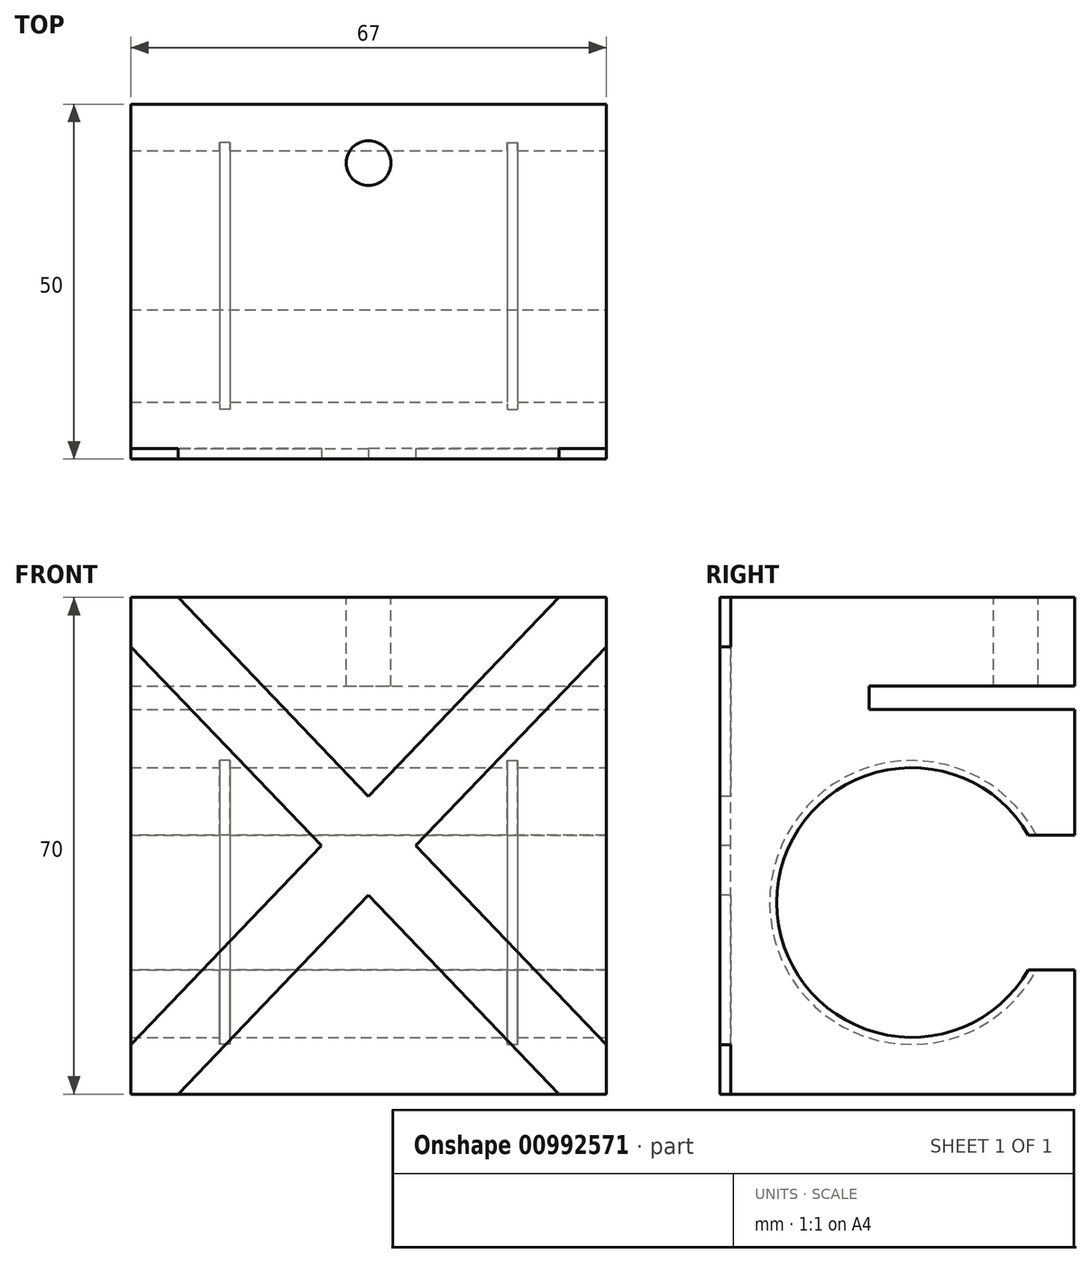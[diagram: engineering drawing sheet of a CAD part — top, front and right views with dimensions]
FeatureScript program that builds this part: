
annotation { "Feature Type Name" : "Feature", "Feature Type Description" : "" }
export const myFeature = defineFeature(function(context is Context, id is Id, definition is map)
    precondition{}
    {
        {
            var Q0;
            Q0=qCreatedBy(makeId("Top.planeOp"),FACE);
            var sketch = newSketch(context, id + "F0", { "sketchPlane" : qUnion([Q0])});
            skLineSegment(sketch, "E0.bottom", {"start": v(33.5, 25) * mm, "end": v(-33.5, 25) * mm});
            skLineSegment(sketch, "E0.top", {"start": v(33.5, -25) * mm, "end": v(-33.5, -25) * mm});
            skLineSegment(sketch, "E0.left", {"start": v(33.5, 25) * mm, "end": v(33.5, -25) * mm});
            skLineSegment(sketch, "E0.right", {"start": v(-33.5, 25) * mm, "end": v(-33.5, -25) * mm});
            skPoint(sketch, "E0.middle", {"position": v(0, 0) * mm});
            skSolve(sketch);
        }
        {
            var Q0;
            Q0 = qSketchRegion(id + "F0", true);
            extrude(context, id + "F1", {"entities" : qUnion([Q0]), "depth" : 70 * mm, "offsetDistance" : 25 * mm});
        }
        {
            var Q0;
            Q0=makeQuery(id+"F1.opExtrude","SWEPT_FACE",FACE,{"disambiguationData":[OSD([sQuery(id+"F0.wireOp",EDGE,"E0.top")])]});
            var sketch = newSketch(context, id + "F2", { "sketchPlane" : qUnion([Q0])});
            skLineSegment(sketch, "E1", {"start": v(-26.86, 70) * mm, "end": v(0, 41.94) * mm});
            skLineSegment(sketch, "E2", {"start": v(33.5, 6.94) * mm, "end": v(33.5, 0) * mm});
            skLineSegment(sketch, "E3", {"start": v(26.86, 0) * mm, "end": v(0, 28.06) * mm});
            skLineSegment(sketch, "E4", {"start": v(-33.5, 63.06) * mm, "end": v(-33.5, 70) * mm});
            skLineSegment(sketch, "E5", {"start": v(-33.5, 0) * mm, "end": v(-33.5, 6.94) * mm});
            skLineSegment(sketch, "E6", {"start": v(-33.5, 6.94) * mm, "end": v(-6.64, 35) * mm});
            skLineSegment(sketch, "E7", {"start": v(26.86, 70) * mm, "end": v(33.5, 70) * mm});
            skLineSegment(sketch, "E8", {"start": v(33.5, 63.06) * mm, "end": v(6.64, 35) * mm});
            skLineSegment(sketch, "E9", {"start": v(-26.86, 0) * mm, "end": v(-33.5, 0) * mm});
            skLineSegment(sketch, "E10.trimOffspring", {"start": v(0, 41.94) * mm, "end": v(26.86, 70) * mm});
            skLineSegment(sketch, "E11.trimOffspring", {"start": v(0, 28.06) * mm, "end": v(-26.86, 0) * mm});
            skLineSegment(sketch, "E12.trimOffspring", {"start": v(-6.64, 35) * mm, "end": v(-33.5, 63.06) * mm});
            skLineSegment(sketch, "E13.trimOffspring", {"start": v(6.64, 35) * mm, "end": v(33.5, 6.94) * mm});
            skSolve(sketch);
        }
        {
            var Q0;
            Q0 = qSketchRegion(id + "F2", true);
            var Q1;
            {var subQ2=sQuery(id+"F2.wireOp",EDGE,"E1");Q1=makeQuery(id+"F2.imprint","IMPRINT",FACE,{"disambiguationData":[TD([[makeQuery(id+"F2.imprint","IMPRINT",EDGE,{"derivedFrom":subQ2}),-1.0]])]});}
            extrude(context, id + "F3", {"entities" : qUnion([Q0, Q1]), "operationType" : NewBodyOperationType.REMOVE, "oppositeDirection" : true, "depth" : 1.5 * mm, "offsetDistance" : 25 * mm});
        }
        {
            var Q0;
            Q0=makeQuery(id+"F1.opExtrude","SWEPT_FACE",FACE,{"disambiguationData":[OSD([sQuery(id+"F0.wireOp",EDGE,"E0.left")])]});
            var sketch = newSketch(context, id + "F4", { "sketchPlane" : qUnion([Q0])});
            skArc(sketch, "E14", {"start": v(18.45, 36.5) * mm, "mid": v(-17, 27) * mm, "end": v(18.45, 17.5) * mm});
            skLineSegment(sketch, "E15.bottom", {"start": v(33.29, 17.5) * mm, "end": v(18.45, 17.5) * mm});
            skLineSegment(sketch, "E15.top", {"start": v(33.29, 36.5) * mm, "end": v(18.45, 36.5) * mm});
            skLineSegment(sketch, "E15.left", {"start": v(33.29, 17.5) * mm, "end": v(33.29, 36.5) * mm});
            skPoint(sketch, "E15.middle", {"position": v(15.05, 27) * mm});
            skPoint(sketch, "E15.right.end.orphan", {"position": v(-3.2, 36.5) * mm});
            skPoint(sketch, "E16.orphan", {"position": v(-3.2, 17.5) * mm});
            skLineSegment(sketch, "E17.bottom", {"start": v(-4, 57.5) * mm, "end": v(54, 57.5) * mm});
            skLineSegment(sketch, "E17.top", {"start": v(-4, 54.2) * mm, "end": v(54, 54.2) * mm});
            skLineSegment(sketch, "E17.left", {"start": v(-4, 57.5) * mm, "end": v(-4, 54.2) * mm});
            skLineSegment(sketch, "E17.right", {"start": v(54, 57.5) * mm, "end": v(54, 54.2) * mm});
            skPoint(sketch, "E17.middle", {"position": v(25, 55.85) * mm});
            skSolve(sketch);
        }
        {
            var Q0;
            Q0 = qSketchRegion(id + "F4", true);
            extrude(context, id + "F5", {"entities" : qUnion([Q0]), "operationType" : NewBodyOperationType.REMOVE, "endBound" : BoundingType.THROUGH_ALL, "oppositeDirection" : true, "depth" : 25 * mm, "offsetDistance" : 25 * mm});
        }
        {
            var Q0;
            Q0 = qSketchRegion(id + "F4", true);
            extrude(context, id + "F6", {"entities" : qUnion([Q0]), "operationType" : NewBodyOperationType.REMOVE, "endBound" : BoundingType.THROUGH_ALL, "oppositeDirection" : true, "depth" : 25 * mm, "offsetDistance" : 25 * mm});
        }
        {
            var Q0;
            Q0=makeQuery(id+"F1.opExtrude","CAP_FACE",FACE,{"disambiguationData":[OSD([sQuery(id+"F0.wireOp",EDGE,"E0.bottom"),sQuery(id+"F0.wireOp",EDGE,"E0.top"),sQuery(id+"F0.wireOp",EDGE,"E0.left"),sQuery(id+"F0.wireOp",EDGE,"E0.right")])],"isStart":false});
            var sketch = newSketch(context, id + "F7", { "sketchPlane" : qUnion([Q0])});
            skCircle(sketch, "E18", {"center": v(0, 16.7) * mm, "radius": 3.15 * mm});
            skSolve(sketch);
        }
        {
            var Q0;
            Q0 = qSketchRegion(id + "F7", true);
            extrude(context, id + "F8", {"entities" : qUnion([Q0]), "operationType" : NewBodyOperationType.REMOVE, "endBound" : BoundingType.UP_TO_NEXT, "oppositeDirection" : true, "depth" : 25 * mm, "offsetDistance" : 25 * mm});
        }
        {
            var Q0;
            Q0=qCreatedBy(makeId("Right.planeOp"),FACE);
            cPlane(context, id + "F9", {"entities" : qUnion([Q0]), "cplaneType" : CPlaneType.OFFSET, "offset" : 21 * mm, "width" : 150 * mm, "height" : 150 * mm});
        }
        {
            var Q0;
            Q0=qCreatedBy(makeId("Right.planeOp"),FACE);
            cPlane(context, id + "F10", {"entities" : qUnion([Q0]), "cplaneType" : CPlaneType.OFFSET, "offset" : 21 * mm, "oppositeDirection" : true, "width" : 150 * mm, "height" : 150 * mm});
        }
        {
            var Q0;
            Q0=qCreatedBy(id+"F9.planeOp",FACE);
            var sketch = newSketch(context, id + "F11", { "sketchPlane" : qUnion([Q0])});
            skCircle(sketch, "E19", {"center": v(2, 27) * mm, "radius": 20 * mm});
            skSolve(sketch);
        }
        {
            var Q0;
            Q0 = qSketchRegion(id + "F11", true);
            extrude(context, id + "F12", {"entities" : qUnion([Q0]), "operationType" : NewBodyOperationType.REMOVE, "oppositeDirection" : true, "depth" : 1.5 * mm, "offsetDistance" : 25 * mm});
        }
        {
            var Q0;
            Q0=qCreatedBy(id+"F10.planeOp",FACE);
            var sketch = newSketch(context, id + "F13", { "sketchPlane" : qUnion([Q0])});
            skCircle(sketch, "E20", {"center": v(2, 27) * mm, "radius": 20 * mm});
            skSolve(sketch);
        }
        {
            var Q0;
            Q0 = qSketchRegion(id + "F13", true);
            extrude(context, id + "F14", {"entities" : qUnion([Q0]), "operationType" : NewBodyOperationType.REMOVE, "depth" : 1.5 * mm, "offsetDistance" : 25 * mm});
        }
    });
